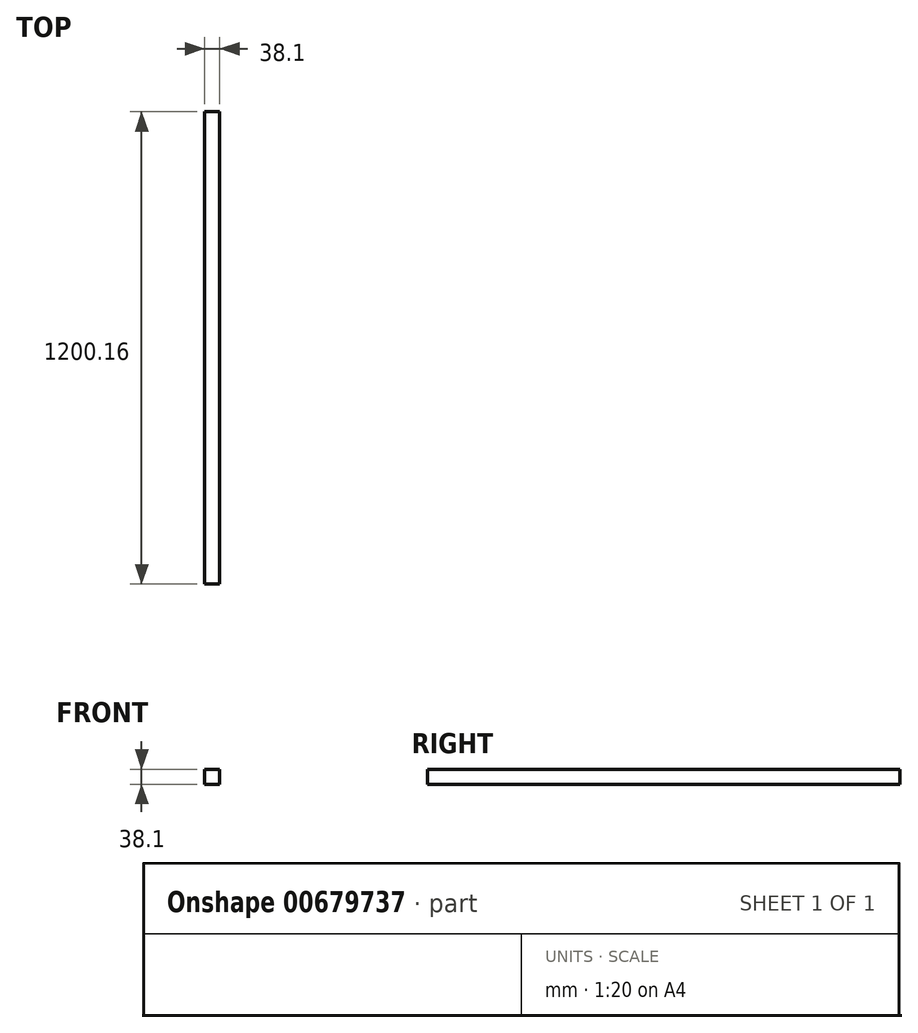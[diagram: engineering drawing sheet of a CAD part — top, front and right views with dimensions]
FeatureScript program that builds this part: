
annotation { "Feature Type Name" : "Feature", "Feature Type Description" : "" }
export const myFeature = defineFeature(function(context is Context, id is Id, definition is map)
    precondition{}
    {
        {
            var Q0;
            Q0=qCreatedBy(makeId("Front.planeOp"),FACE);
            var sketch = newSketch(context, id + "F0", { "sketchPlane" : qUnion([Q0])});
            skLineSegment(sketch, "E0.bottom", {"start": v(-19.05, 19.05) * mm, "end": v(19.05, 19.05) * mm});
            skLineSegment(sketch, "E0.top", {"start": v(-19.05, -19.05) * mm, "end": v(19.05, -19.05) * mm});
            skLineSegment(sketch, "E0.left", {"start": v(-19.05, 19.05) * mm, "end": v(-19.05, -19.05) * mm});
            skLineSegment(sketch, "E0.right", {"start": v(19.05, 19.05) * mm, "end": v(19.05, -19.05) * mm});
            skPoint(sketch, "E0.middle", {"position": v(0, 0) * mm});
            skSolve(sketch);
        }
        {
            var Q0;
            Q0=makeQuery(id+"F0.imprint","IMPRINT",FACE,{"disambiguationData":[TD([[makeQuery(id+"F0.imprint","IMPRINT",EDGE,{"derivedFrom":sQuery(id+"F0.wireOp",EDGE,"E0.bottom")}),-1.0]])]});
            extrude(context, id + "F1", {"entities" : qUnion([Q0]), "endBound" : BoundingType.SYMMETRIC, "depth" : 1200.15 * mm, "offsetDistance" : 25.4 * mm});
        }
    });
